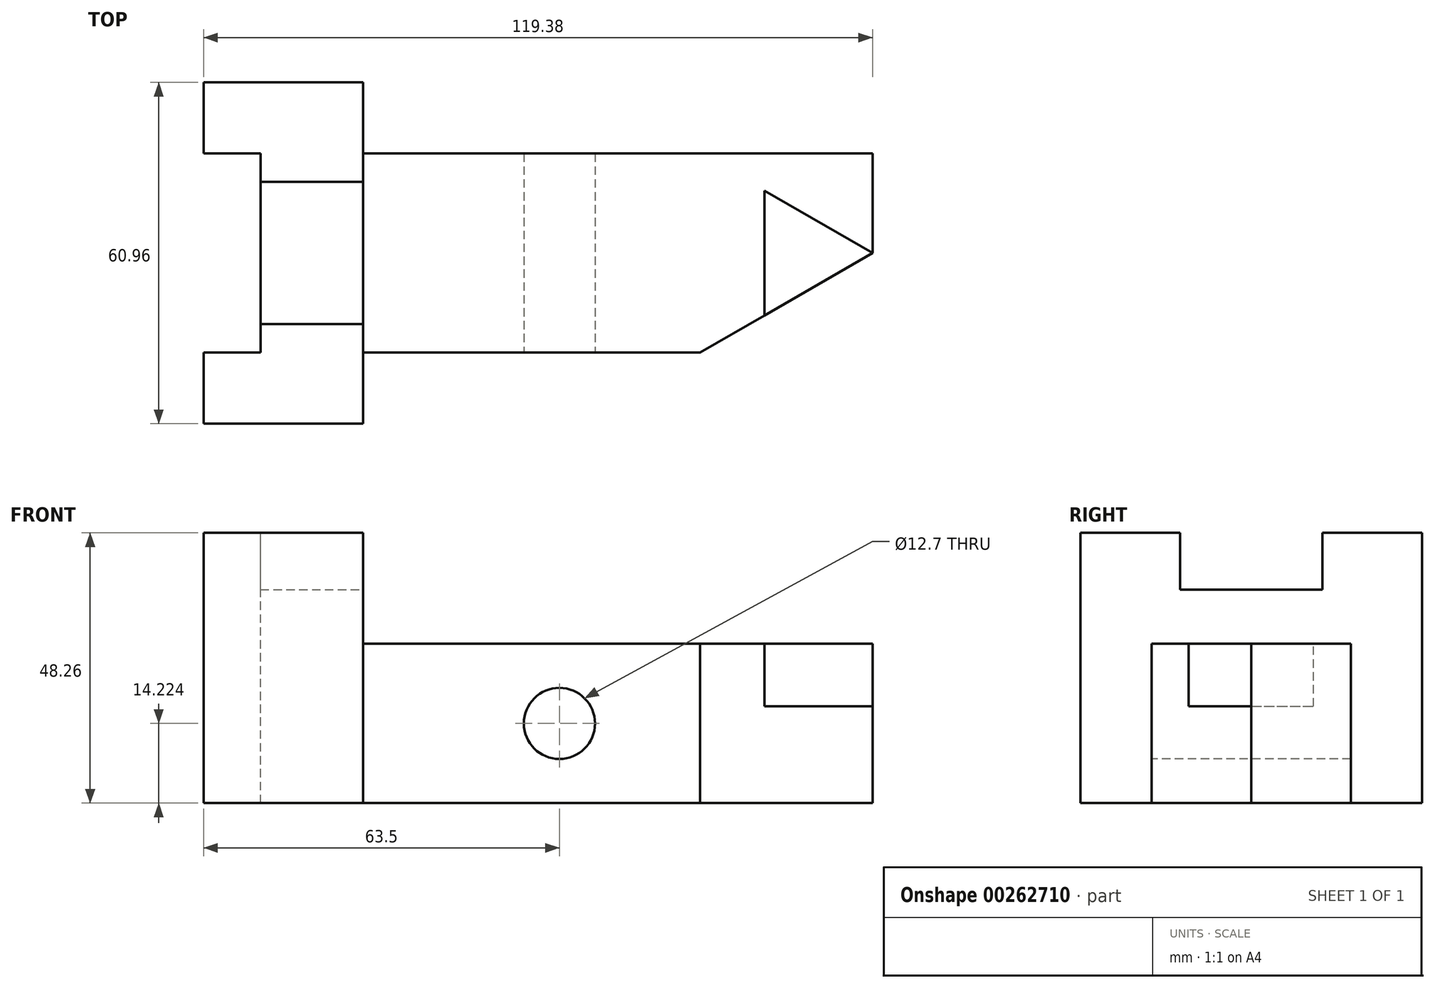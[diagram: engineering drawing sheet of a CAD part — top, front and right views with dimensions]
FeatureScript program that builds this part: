
annotation { "Feature Type Name" : "Feature", "Feature Type Description" : "" }
export const myFeature = defineFeature(function(context is Context, id is Id, definition is map)
    precondition{}
    {
        {
            var Q0;
            Q0=qCreatedBy(makeId("Top.planeOp"),FACE);
            var sketch = newSketch(context, id + "F0", { "sketchPlane" : qUnion([Q0])});
            skLineSegment(sketch, "E0.bottom", {"start": v(-59.69, 30.48) * mm, "end": v(59.7, 30.48) * mm});
            skLineSegment(sketch, "E0.top", {"start": v(-59.7, -30.48) * mm, "end": v(59.7, -30.48) * mm});
            skLineSegment(sketch, "E0.left", {"start": v(-59.69, 30.48) * mm, "end": v(-59.7, -30.48) * mm});
            skLineSegment(sketch, "E0.right", {"start": v(59.7, 30.48) * mm, "end": v(59.69, -30.48) * mm});
            skPoint(sketch, "E0.middle", {"position": v(0, 0) * mm});
            skSolve(sketch);
        }
        {
            var Q0;
            Q0=makeQuery(id+"F0.imprint","IMPRINT",FACE,{"disambiguationData":[TD([[makeQuery(id+"F0.imprint","IMPRINT",EDGE,{"derivedFrom":sQuery(id+"F0.wireOp",EDGE,"E0.bottom")}),-1.0]])]});
            extrude(context, id + "F1", {"entities" : qUnion([Q0]), "endBound" : BoundingType.SYMMETRIC, "depth" : 48.26 * mm});
        }
        {
            var Q0;
            Q0=makeQuery(id+"F1.opExtrude","SWEPT_FACE",FACE,{"disambiguationData":[OSD([sQuery(id+"F0.wireOp",EDGE,"E0.right")])]});
            var sketch = newSketch(context, id + "F2", { "sketchPlane" : qUnion([Q0])});
            skLineSegment(sketch, "E1", {"start": v(-17.78, -24.13) * mm, "end": v(-30.48, -24.13) * mm});
            skLineSegment(sketch, "E2", {"start": v(-30.48, -24.13) * mm, "end": v(-30.48, 24.13) * mm});
            skLineSegment(sketch, "E3", {"start": v(-30.48, 24.13) * mm, "end": v(30.48, 24.13) * mm});
            skLineSegment(sketch, "E4", {"start": v(30.48, 24.13) * mm, "end": v(30.48, -24.13) * mm});
            skLineSegment(sketch, "E5", {"start": v(30.48, -24.13) * mm, "end": v(17.78, -24.13) * mm});
            skLineSegment(sketch, "E6", {"start": v(17.78, -24.13) * mm, "end": v(17.78, 4.32) * mm});
            skLineSegment(sketch, "E7", {"start": v(17.78, 4.32) * mm, "end": v(-17.78, 4.32) * mm});
            skLineSegment(sketch, "E8", {"start": v(-17.78, 4.32) * mm, "end": v(-17.78, -24.13) * mm});
            skSolve(sketch);
        }
        {
            var Q0;
            Q0=makeQuery(id+"F2.imprint","IMPRINT",FACE,{"disambiguationData":[TD([[makeQuery(id+"F2.imprint","IMPRINT",EDGE,{"derivedFrom":sQuery(id+"F2.wireOp",EDGE,"E1")}),-1.0]])]});
            extrude(context, id + "F3", {"entities" : qUnion([Q0]), "operationType" : NewBodyOperationType.REMOVE, "oppositeDirection" : true, "depth" : 90.93 * mm});
        }
        {
            var Q0;
            Q0=makeQuery(id+"F3.boolean.opBoolean","COPY",FACE,{"derivedFrom":makeQuery(id+"F3.opExtrude","CAP_FACE",FACE,{"disambiguationData":[OSD([sQuery(id+"F2.wireOp",EDGE,"E1"),sQuery(id+"F2.wireOp",EDGE,"E2"),sQuery(id+"F2.wireOp",EDGE,"E3"),sQuery(id+"F2.wireOp",EDGE,"E4"),sQuery(id+"F2.wireOp",EDGE,"E5"),sQuery(id+"F2.wireOp",EDGE,"E6"),sQuery(id+"F2.wireOp",EDGE,"E7"),sQuery(id+"F2.wireOp",EDGE,"E8")])],"isStart":false})});
            var sketch = newSketch(context, id + "F4", { "sketchPlane" : qUnion([Q0])});
            skLineSegment(sketch, "E9", {"start": v(-12.7, 24.13) * mm, "end": v(-12.7, 13.97) * mm});
            skLineSegment(sketch, "E10", {"start": v(-12.7, 13.97) * mm, "end": v(12.7, 13.97) * mm});
            skLineSegment(sketch, "E11", {"start": v(12.7, 13.97) * mm, "end": v(12.7, 24.13) * mm});
            skSolve(sketch);
        }
        {
            var Q0;
            {var subQ0=sQuery(id+"F4.wireOp",EDGE,"E9");Q0=makeQuery(id+"F4.imprint","IMPRINT",FACE,{"disambiguationData":[TD([[makeQuery(id+"F4.imprint","IMPRINT",EDGE,{"derivedFrom":subQ0}),1.0]])]});}
            extrude(context, id + "F5", {"entities" : qUnion([Q0]), "operationType" : NewBodyOperationType.REMOVE, "oppositeDirection" : true, "depth" : 45.4 * mm});
        }
        {
            var Q0;
            {var subQ0=sQuery(id+"F0.wireOp",EDGE,"E0.top");var subQ1=sQuery(id+"F0.wireOp",EDGE,"E0.left");Q0=makeQuery(id+"F5.boolean.opBoolean","SPLIT",FACE,{"disambiguationData":[TD([makeQuery(id+"F1.opExtrude","SWEPT_FACE",FACE,{"disambiguationData":[OSD([subQ0])]})])],"derivedFrom":makeQuery(id+"F1.opExtrude","CAP_FACE",FACE,{"disambiguationData":[OSD([sQuery(id+"F0.wireOp",EDGE,"E0.bottom"),subQ0,subQ1,sQuery(id+"F0.wireOp",EDGE,"E0.right")])],"isStart":false})});}
            var sketch = newSketch(context, id + "F6", { "sketchPlane" : qUnion([Q0])});
            skLineSegment(sketch, "E12", {"start": v(-59.7, -17.78) * mm, "end": v(-49.53, -17.78) * mm});
            skLineSegment(sketch, "E13", {"start": v(-49.53, -17.78) * mm, "end": v(-49.53, 17.78) * mm});
            skLineSegment(sketch, "E14", {"start": v(-49.53, 17.78) * mm, "end": v(-59.69, 17.78) * mm});
            skLineSegment(sketch, "E15", {"start": v(-59.7, -17.78) * mm, "end": v(-59.7, 17.78) * mm});
            skSolve(sketch);
        }
        {
            var Q0;
            {var subQ0=sQuery(id+"F6.wireOp",EDGE,"E12");Q0=makeQuery(id+"F6.imprint","IMPRINT",FACE,{"disambiguationData":[TD([[makeQuery(id+"F6.imprint","IMPRINT",EDGE,{"derivedFrom":subQ0}),1.0]])]});}
            var Q1;
            {var subQ0=sQuery(id+"F6.wireOp",EDGE,"E14");Q1=makeQuery(id+"F6.imprint","IMPRINT",FACE,{"disambiguationData":[TD([[makeQuery(id+"F6.imprint","IMPRINT",EDGE,{"derivedFrom":subQ0}),1.0]])]});}
            extrude(context, id + "F7", {"entities" : qUnion([Q0, Q1]), "operationType" : NewBodyOperationType.REMOVE, "oppositeDirection" : true, "depth" : 53.42 * mm});
        }
        {
            var Q0;
            Q0=makeQuery(id+"F3.boolean.opBoolean","COPY",FACE,{"derivedFrom":makeQuery(id+"F3.opExtrude","SWEPT_FACE",FACE,{"disambiguationData":[OSD([sQuery(id+"F2.wireOp",EDGE,"E7")])]})});
            var sketch = newSketch(context, id + "F8", { "sketchPlane" : qUnion([Q0])});
            skLineSegment(sketch, "E16", {"start": v(59.7, 0) * mm, "end": v(28.9, 17.78) * mm});
            skLineSegment(sketch, "E17", {"start": v(28.9, 17.78) * mm, "end": v(59.7, 0) * mm});
            skLineSegment(sketch, "E18", {"start": v(59.7, 0) * mm, "end": v(28.9, -17.78) * mm});
            skSolve(sketch);
        }
        {
            var Q0;
            {var subQ0=sQuery(id+"F8.wireOp",EDGE,"E17");Q0=makeQuery(id+"F8.imprint","IMPRINT",FACE,{"disambiguationData":[TD([[makeQuery(id+"F8.imprint","IMPRINT",EDGE,{"derivedFrom":subQ0}),1.0]])]});}
            var Q1;
            {var subQ0=sQuery(id+"F8.wireOp",EDGE,"E18");Q1=makeQuery(id+"F8.imprint","IMPRINT",FACE,{"disambiguationData":[TD([[makeQuery(id+"F8.imprint","IMPRINT",EDGE,{"derivedFrom":subQ0}),1.0]])]});}
            extrude(context, id + "F9", {"entities" : qUnion([Q0, Q1]), "operationType" : NewBodyOperationType.REMOVE, "oppositeDirection" : true, "depth" : 34.8 * mm});
        }
        {
            var Q0;
            Q0=makeQuery(id+"F3.boolean.opBoolean","COPY",FACE,{"derivedFrom":makeQuery(id+"F3.opExtrude","SWEPT_FACE",FACE,{"disambiguationData":[OSD([sQuery(id+"F2.wireOp",EDGE,"E7")])]})});
            var sketch = newSketch(context, id + "F10", { "sketchPlane" : qUnion([Q0])});
            skLineSegment(sketch, "E19", {"start": v(40.39, -11.15) * mm, "end": v(40.39, 11.15) * mm});
            skLineSegment(sketch, "E20", {"start": v(40.39, -11.15) * mm, "end": v(59.7, 0) * mm});
            skLineSegment(sketch, "E21", {"start": v(59.7, 0) * mm, "end": v(40.39, 11.15) * mm});
            skSolve(sketch);
        }
        {
            var Q0;
            Q0=makeQuery(id+"F10.imprint","IMPRINT",FACE,{"disambiguationData":[TD([[makeQuery(id+"F10.imprint","IMPRINT",EDGE,{"derivedFrom":sQuery(id+"F10.wireOp",EDGE,"E19")}),-1.0]])]});
            extrude(context, id + "F11", {"entities" : qUnion([Q0]), "operationType" : NewBodyOperationType.REMOVE, "oppositeDirection" : true, "depth" : 11.18 * mm});
        }
        {
            var Q0;
            Q0=makeQuery(id+"F3.boolean.opBoolean","COPY",FACE,{"derivedFrom":makeQuery(id+"F3.opExtrude","SWEPT_FACE",FACE,{"disambiguationData":[OSD([sQuery(id+"F2.wireOp",EDGE,"E8")])]})});
            var sketch = newSketch(context, id + "F12", { "sketchPlane" : qUnion([Q0])});
            skCircle(sketch, "E22", {"center": v(3.8, -9.9) * mm, "radius": 6.35 * mm});
            skSolve(sketch);
        }
        {
            var Q0;
            Q0=makeQuery(id+"F12.imprint","IMPRINT",FACE,{"disambiguationData":[TD([[makeQuery(id+"F12.imprint","IMPRINT",EDGE,{"derivedFrom":sQuery(id+"F12.wireOp",EDGE,"E22")}),1.0]])]});
            extrude(context, id + "F13", {"entities" : qUnion([Q0]), "operationType" : NewBodyOperationType.REMOVE, "oppositeDirection" : true, "depth" : 58.17 * mm});
        }
    });
